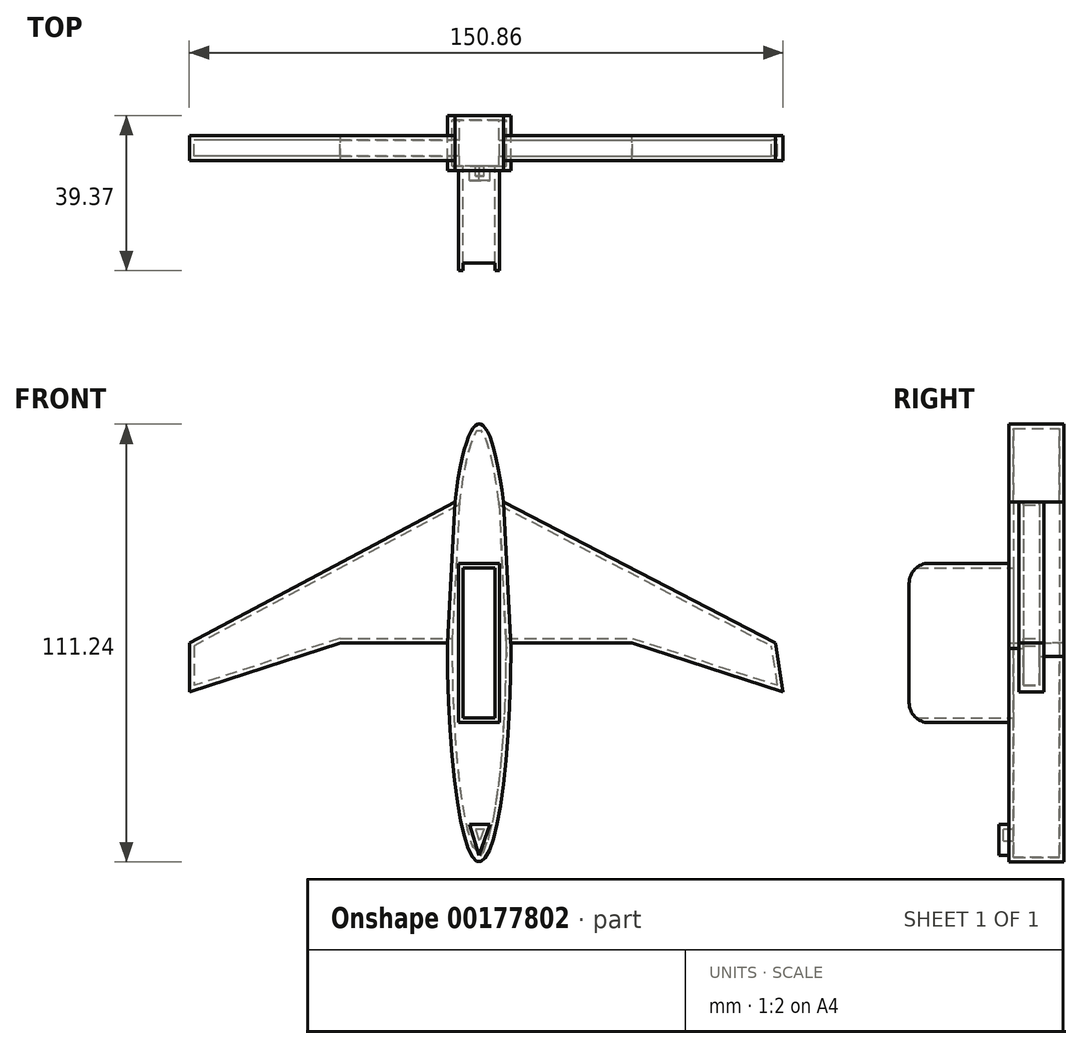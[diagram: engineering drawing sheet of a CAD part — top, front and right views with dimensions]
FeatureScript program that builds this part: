
annotation { "Feature Type Name" : "Feature", "Feature Type Description" : "" }
export const myFeature = defineFeature(function(context is Context, id is Id, definition is map)
    precondition{}
    {
        {
            var Q0;
            Q0=qCreatedBy(makeId("Front.planeOp"),FACE);
            var sketch = newSketch(context, id + "F0", { "sketchPlane" : qUnion([Q0])});
            skEllipse(sketch, "E0", {"center": v(0, 0) * mm, "majorRadius": 55.62 * mm, "minorRadius": 8.05 * mm, "majorAxis": v(0, 1)});
            skLineSegment(sketch, "E1", {"start": v(-6.17, 35.78) * mm, "end": v(-73.63, 0) * mm});
            skLineSegment(sketch, "E2", {"start": v(6.17, 35.78) * mm, "end": v(75.26, 0) * mm});
            skLineSegment(sketch, "E3", {"start": v(-73.63, 0) * mm, "end": v(-73.63, -12.38) * mm});
            skLineSegment(sketch, "E4", {"start": v(-7.85, -12.38) * mm, "end": v(7.85, -12.38) * mm});
            skLineSegment(sketch, "E5", {"start": v(77.23, -12.38) * mm, "end": v(75.26, 0) * mm});
            skLineSegment(sketch, "E6", {"start": v(-35.16, 0) * mm, "end": v(-73.63, -12.38) * mm});
            skLineSegment(sketch, "E7", {"start": v(-35.16, 0) * mm, "end": v(-8.05, 0) * mm});
            skLineSegment(sketch, "E8", {"start": v(-8.05, 0) * mm, "end": v(0, 0) * mm});
            skLineSegment(sketch, "E9", {"start": v(8.05, 0) * mm, "end": v(38.76, 0) * mm});
            skLineSegment(sketch, "E10", {"start": v(38.76, 0) * mm, "end": v(77.23, -12.38) * mm});
            skSolve(sketch);
        }
        {
            var Q0;
            Q0 = qSketchRegion(id + "F0", true);
            extrude(context, id + "F1", {"entities" : qUnion([Q0]), "depth" : 6.35 * mm});
        }
        {
            var Q0;
            Q0=makeQuery(id+"F1.opExtrude","CAP_FACE",FACE,{"disambiguationData":[OSD([sQuery(id+"F0.wireOp",EDGE,"E0"),sQuery(id+"F0.wireOp",EDGE,"E1"),sQuery(id+"F0.wireOp",EDGE,"E2"),sQuery(id+"F0.wireOp",EDGE,"E3"),sQuery(id+"F0.wireOp",EDGE,"E5"),sQuery(id+"F0.wireOp",EDGE,"E6"),sQuery(id+"F0.wireOp",EDGE,"E7"),sQuery(id+"F0.wireOp",EDGE,"E9"),sQuery(id+"F0.wireOp",EDGE,"E10")])],"isStart":false});
            var sketch = newSketch(context, id + "F2", { "sketchPlane" : qUnion([Q0])});
            skLineSegment(sketch, "E11", {"start": v(-6.17, 35.78) * mm, "end": v(-8.05, 0) * mm});
            skLineSegment(sketch, "E12", {"start": v(6.17, 35.78) * mm, "end": v(8.05, -1.38) * mm});
            skSolve(sketch);
        }
        {
            var Q0;
            Q0 = qSketchRegion(id + "F2", true);
            var Q1;
            {var subQ0=sQuery(id+"F2.wireOp",EDGE,"E11");Q1=makeQuery(id+"F2.imprint","IMPRINT",FACE,{"disambiguationData":[TD([[makeQuery(id+"F2.imprint","IMPRINT",EDGE,{"derivedFrom":subQ0}),1.0]])]});}
            extrude(context, id + "F3", {"entities" : qUnion([Q0, Q1]), "operationType" : NewBodyOperationType.ADD, "depth" : 2.54 * mm});
        }
        {
            var Q0;
            Q0=makeQuery(id+"F1.opExtrude","CAP_FACE",FACE,{"disambiguationData":[OSD([sQuery(id+"F0.wireOp",EDGE,"E0"),sQuery(id+"F0.wireOp",EDGE,"E1"),sQuery(id+"F0.wireOp",EDGE,"E2"),sQuery(id+"F0.wireOp",EDGE,"E3"),sQuery(id+"F0.wireOp",EDGE,"E5"),sQuery(id+"F0.wireOp",EDGE,"E6"),sQuery(id+"F0.wireOp",EDGE,"E7"),sQuery(id+"F0.wireOp",EDGE,"E9"),sQuery(id+"F0.wireOp",EDGE,"E10")])],"isStart":true});
            var sketch = newSketch(context, id + "F4", { "sketchPlane" : qUnion([Q0])});
            skLineSegment(sketch, "E13", {"start": v(-6.17, 35.78) * mm, "end": v(-8.04, -3.4) * mm});
            skLineSegment(sketch, "E14", {"start": v(6.17, 35.78) * mm, "end": v(8.05, 0) * mm});
            skSolve(sketch);
        }
        {
            var Q0;
            Q0 = qSketchRegion(id + "F4", true);
            var Q1;
            {var subQ0=sQuery(id+"F4.wireOp",EDGE,"E13");Q1=makeQuery(id+"F4.imprint","IMPRINT",FACE,{"disambiguationData":[TD([[makeQuery(id+"F4.imprint","IMPRINT",EDGE,{"derivedFrom":subQ0}),1.0]])]});}
            extrude(context, id + "F5", {"entities" : qUnion([Q0, Q1]), "operationType" : NewBodyOperationType.ADD, "depth" : 5.08 * mm});
        }
        {
            var Q0;
            Q0=makeQuery(id+"F3.opExtrude","CAP_FACE",FACE,{"disambiguationData":[OSD([sQuery(id+"F0.wireOp",EDGE,"E0"),sQuery(id+"F2.wireOp",EDGE,"E11"),sQuery(id+"F2.wireOp",EDGE,"E12")])],"isStart":false});
            var sketch = newSketch(context, id + "F6", { "sketchPlane" : qUnion([Q0])});
            skLineSegment(sketch, "E15", {"start": v(-2.51, -46.07) * mm, "end": v(2.8, -46.07) * mm});
            skLineSegment(sketch, "E16", {"start": v(2.8, -46.07) * mm, "end": v(0, -53.9) * mm});
            skLineSegment(sketch, "E17", {"start": v(0, -53.9) * mm, "end": v(-2.51, -46.07) * mm});
            skSolve(sketch);
        }
        {
            var Q0;
            Q0 = qSketchRegion(id + "F6", true);
            extrude(context, id + "F7", {"entities" : qUnion([Q0]), "operationType" : NewBodyOperationType.ADD, "depth" : 2.54 * mm});
        }
        {
            var Q0;
            Q0=makeQuery(id+"F3.opExtrude","CAP_FACE",FACE,{"disambiguationData":[OSD([sQuery(id+"F0.wireOp",EDGE,"E0"),sQuery(id+"F2.wireOp",EDGE,"E11"),sQuery(id+"F2.wireOp",EDGE,"E12")])],"isStart":false});
            var sketch = newSketch(context, id + "F8", { "sketchPlane" : qUnion([Q0])});
            skLineSegment(sketch, "E18.bottom", {"start": v(5.21, 20.25) * mm, "end": v(-5.21, 20.25) * mm});
            skLineSegment(sketch, "E18.top", {"start": v(5.21, -20.25) * mm, "end": v(-5.21, -20.25) * mm});
            skLineSegment(sketch, "E18.left", {"start": v(5.21, 20.25) * mm, "end": v(5.21, -20.25) * mm});
            skLineSegment(sketch, "E18.right", {"start": v(-5.21, 20.25) * mm, "end": v(-5.21, -20.25) * mm});
            skPoint(sketch, "E18.middle", {"position": v(0, 0) * mm});
            skSolve(sketch);
        }
        {
            var Q0;
            Q0 = qSketchRegion(id + "F8", true);
            extrude(context, id + "F9", {"entities" : qUnion([Q0]), "operationType" : NewBodyOperationType.ADD, "depth" : 25.4 * mm});
        }
        {
            var Q0;
            Q0=makeQuery(id+"F9.opExtrude","CAP_FACE",FACE,{"disambiguationData":[OSD([sQuery(id+"F8.wireOp",EDGE,"E18.bottom"),sQuery(id+"F8.wireOp",EDGE,"E18.top"),sQuery(id+"F8.wireOp",EDGE,"E18.left"),sQuery(id+"F8.wireOp",EDGE,"E18.right")])],"isStart":false});
            shell(context, id + "F10", {"entities" : qUnion([Q0]), "thickness" : 1.14 * mm});
        }
        {
            var Q0;
            Q0=makeQuery(id+"F9.opExtrude","CAP_EDGE",EDGE,{"disambiguationData":[OSD([sQuery(id+"F8.wireOp",EDGE,"E18.bottom")])],"isStart":false});
            var Q1;
            Q1=makeQuery(id+"F9.opExtrude","CAP_EDGE",EDGE,{"disambiguationData":[OSD([sQuery(id+"F8.wireOp",EDGE,"E18.top")])],"isStart":false});
            fillet(context, id + "F11", {"entities" : qUnion([Q0, Q1]), "radius" : 5.08 * mm, "tangentPropagation" : true, "allowEdgeOverflow" : false});
        }
    });
